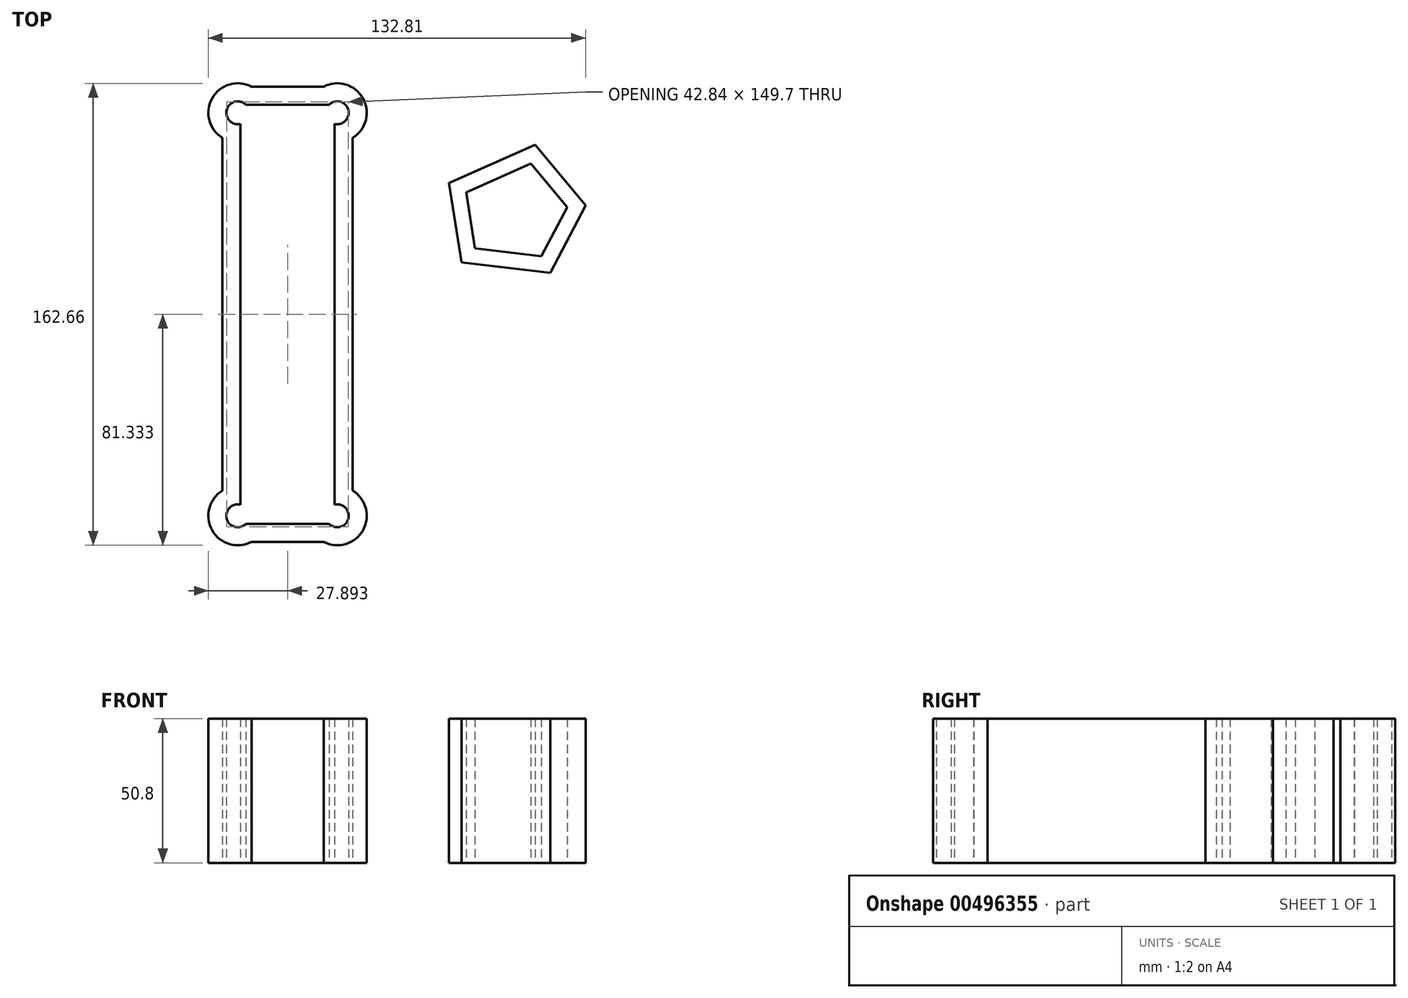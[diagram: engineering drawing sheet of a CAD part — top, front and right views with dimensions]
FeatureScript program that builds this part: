
annotation { "Feature Type Name" : "Feature", "Feature Type Description" : "" }
export const myFeature = defineFeature(function(context is Context, id is Id, definition is map)
    precondition{}
    {
        {
            var Q0;
            Q0=qCreatedBy(makeId("Top.planeOp"),FACE);
            var sketch = newSketch(context, id + "F0", { "sketchPlane" : qUnion([Q0])});
            skLineSegment(sketch, "E0", {"start": v(-84.14, -59.72) * mm, "end": v(-84.14, 2.36) * mm});
            skLineSegment(sketch, "E1", {"start": v(-73.94, 20.43) * mm, "end": v(-61.24, 20.43) * mm});
            skArc(sketch, "E2", {"start": v(-73.94, 20.43) * mm, "mid": v(-87.79, 16.34) * mm, "end": v(-84.14, 2.36) * mm});
            skLineSegment(sketch, "E3.MirrorCS", {"start": v(-38.33, -59.72) * mm, "end": v(-38.33, 2.36) * mm});
            skLineSegment(sketch, "E4.MirrorCS", {"start": v(-48.54, 20.43) * mm, "end": v(-61.24, 20.43) * mm});
            skArc(sketch, "E5.MirrorCS", {"start": v(-48.54, 20.43) * mm, "mid": v(-34.68, 16.34) * mm, "end": v(-38.33, 2.36) * mm});
            skLineSegment(sketch, "E6.MirrorCS", {"start": v(-38.33, -59.72) * mm, "end": v(-38.33, -121.8) * mm});
            skArc(sketch, "E7.MirrorCS", {"start": v(-48.54, -139.86) * mm, "mid": v(-34.68, -135.77) * mm, "end": v(-38.33, -121.8) * mm});
            skLineSegment(sketch, "E8.MirrorCS", {"start": v(-48.54, -139.86) * mm, "end": v(-61.24, -139.86) * mm});
            skLineSegment(sketch, "E9.MirrorCS", {"start": v(-84.14, -59.72) * mm, "end": v(-84.14, -121.8) * mm});
            skLineSegment(sketch, "E10.MirrorCS", {"start": v(-73.94, -139.86) * mm, "end": v(-61.24, -139.86) * mm});
            skArc(sketch, "E11.MirrorCS", {"start": v(-73.94, -139.86) * mm, "mid": v(-87.79, -135.77) * mm, "end": v(-84.14, -121.8) * mm});
            skLineSegment(sketch, "E12.0", {"start": v(-77.79, -59.72) * mm, "end": v(-77.79, -126.76) * mm});
            skArc(sketch, "E12.1", {"start": v(-46.57, 14.08) * mm, "mid": v(-39.84, 12.32) * mm, "end": v(-44.68, 7.32) * mm});
            skLineSegment(sketch, "E12.2", {"start": v(-46.57, 14.08) * mm, "end": v(-61.24, 14.08) * mm});
            skLineSegment(sketch, "E12.3", {"start": v(-75.9, 14.08) * mm, "end": v(-61.24, 14.08) * mm});
            skArc(sketch, "E12.4", {"start": v(-75.9, 14.08) * mm, "mid": v(-82.63, 12.32) * mm, "end": v(-77.79, 7.32) * mm});
            skLineSegment(sketch, "E12.5", {"start": v(-44.68, -59.72) * mm, "end": v(-44.68, 7.32) * mm});
            skLineSegment(sketch, "E12.6", {"start": v(-77.79, -59.72) * mm, "end": v(-77.79, 7.32) * mm});
            skLineSegment(sketch, "E12.7", {"start": v(-44.68, -59.72) * mm, "end": v(-44.68, -126.76) * mm});
            skArc(sketch, "E12.8", {"start": v(-46.57, -133.51) * mm, "mid": v(-39.84, -131.75) * mm, "end": v(-44.68, -126.76) * mm});
            skLineSegment(sketch, "E12.9", {"start": v(-46.57, -133.51) * mm, "end": v(-61.24, -133.51) * mm});
            skLineSegment(sketch, "E12.10", {"start": v(-75.9, -133.51) * mm, "end": v(-61.24, -133.51) * mm});
            skArc(sketch, "E12.11", {"start": v(-75.9, -133.51) * mm, "mid": v(-82.63, -131.75) * mm, "end": v(-77.79, -126.76) * mm});
            skSolve(sketch);
        }
        {
            var Q0;
            Q0=makeQuery(id+"F0.imprint","IMPRINT",FACE,{"disambiguationData":[TD([[makeQuery(id+"F0.imprint","IMPRINT",EDGE,{"derivedFrom":sQuery(id+"F0.wireOp",EDGE,"E0")}),-1.0]])]});
            extrude(context, id + "F1", {"entities" : qUnion([Q0]), "depth" : 50.8 * mm});
        }
        {
            var Q0;
            Q0=qCreatedBy(makeId("Top.planeOp"),FACE);
            var sketch = newSketch(context, id + "F2", { "sketchPlane" : qUnion([Q0])});
            skLineSegment(sketch, "E13", {"start": v(0, -41.4) * mm, "end": v(31.23, -45.16) * mm});
            skLineSegment(sketch, "E14", {"start": v(31.23, -45.16) * mm, "end": v(43.68, -21.36) * mm});
            skLineSegment(sketch, "E15", {"start": v(43.68, -21.36) * mm, "end": v(25.97, 0) * mm});
            skLineSegment(sketch, "E16", {"start": v(25.97, 0) * mm, "end": v(-4.37, -13.55) * mm});
            skLineSegment(sketch, "E17", {"start": v(0, -41.4) * mm, "end": v(-4.37, -13.55) * mm});
            skLineSegment(sketch, "E18.0", {"start": v(24.42, -6.63) * mm, "end": v(1.63, -16.81) * mm});
            skLineSegment(sketch, "E18.1", {"start": v(37.2, -22.05) * mm, "end": v(24.42, -6.63) * mm});
            skLineSegment(sketch, "E18.2", {"start": v(4.72, -36.5) * mm, "end": v(1.63, -16.81) * mm});
            skLineSegment(sketch, "E18.3", {"start": v(4.72, -36.5) * mm, "end": v(28.16, -39.33) * mm});
            skLineSegment(sketch, "E18.4", {"start": v(28.16, -39.33) * mm, "end": v(37.2, -22.05) * mm});
            skSolve(sketch);
        }
        {
            var Q0;
            Q0 = qSketchRegion(id + "F2", true);
            extrude(context, id + "F3", {"entities" : qUnion([Q0]), "depth" : 50.8 * mm});
        }
    });
